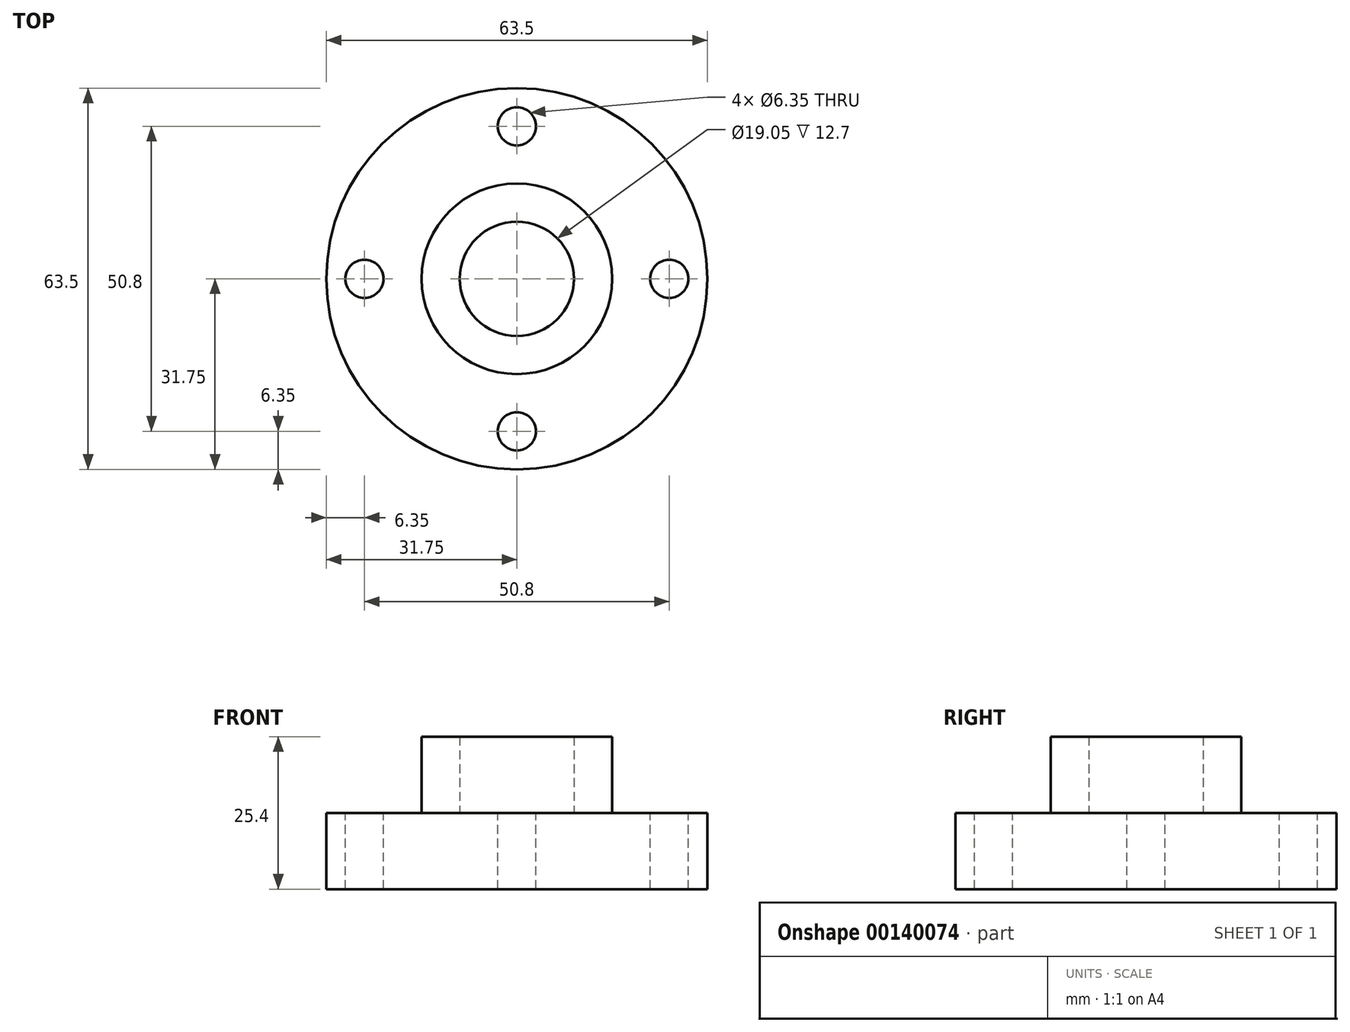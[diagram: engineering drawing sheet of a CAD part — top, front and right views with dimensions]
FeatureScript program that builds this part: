
annotation { "Feature Type Name" : "Feature", "Feature Type Description" : "" }
export const myFeature = defineFeature(function(context is Context, id is Id, definition is map)
    precondition{}
    {
        {
            var Q0;
            Q0=qCreatedBy(makeId("Top.planeOp"),FACE);
            var sketch = newSketch(context, id + "F0", { "sketchPlane" : qUnion([Q0])});
            skCircle(sketch, "E0", {"center": v(0, 0) * mm, "radius": 31.75 * mm});
            skSolve(sketch);
        }
        {
            var Q0;
            Q0 = qSketchRegion(id + "F0", true);
            extrude(context, id + "F1", {"entities" : qUnion([Q0]), "depth" : 12.7 * mm});
        }
        {
            var Q0;
            Q0=makeQuery(id+"F1.opExtrude","CAP_FACE",FACE,{"disambiguationData":[OSD([sQuery(id+"F0.wireOp",EDGE,"E0")])],"isStart":false});
            var sketch = newSketch(context, id + "F2", { "sketchPlane" : qUnion([Q0])});
            skCircle(sketch, "E1", {"center": v(0, 0) * mm, "radius": 15.88 * mm});
            skCircle(sketch, "E2", {"center": v(0, 0) * mm, "radius": 9.53 * mm});
            skCircle(sketch, "E3", {"center": v(-25.4, 0) * mm, "radius": 3.18 * mm});
            skCircle(sketch, "E4", {"center": v(0, 25.4) * mm, "radius": 3.18 * mm});
            skCircle(sketch, "E5", {"center": v(25.4, 0) * mm, "radius": 3.18 * mm});
            skCircle(sketch, "E6", {"center": v(0, -25.4) * mm, "radius": 3.18 * mm});
            skSolve(sketch);
        }
        {
            var Q0;
            Q0=makeQuery(id+"F2.imprint","IMPRINT",FACE,{"disambiguationData":[TD([[makeQuery(id+"F2.imprint","IMPRINT",EDGE,{"derivedFrom":sQuery(id+"F2.wireOp",EDGE,"E3")}),1.0]])]});
            var Q1;
            Q1=makeQuery(id+"F2.imprint","IMPRINT",FACE,{"disambiguationData":[TD([[makeQuery(id+"F2.imprint","IMPRINT",EDGE,{"derivedFrom":sQuery(id+"F2.wireOp",EDGE,"E6")}),1.0]])]});
            var Q2;
            Q2=makeQuery(id+"F2.imprint","IMPRINT",FACE,{"disambiguationData":[TD([[makeQuery(id+"F2.imprint","IMPRINT",EDGE,{"derivedFrom":sQuery(id+"F2.wireOp",EDGE,"E5")}),1.0]])]});
            var Q3;
            Q3=makeQuery(id+"F2.imprint","IMPRINT",FACE,{"disambiguationData":[TD([[makeQuery(id+"F2.imprint","IMPRINT",EDGE,{"derivedFrom":sQuery(id+"F2.wireOp",EDGE,"E4")}),1.0]])]});
            extrude(context, id + "F3", {"entities" : qUnion([Q0, Q1, Q2, Q3]), "operationType" : NewBodyOperationType.REMOVE, "endBound" : BoundingType.THROUGH_ALL, "oppositeDirection" : true, "depth" : 25.4 * mm});
        }
        {
            var Q0;
            Q0=makeQuery(id+"F2.imprint","IMPRINT",FACE,{"disambiguationData":[TD([[makeQuery(id+"F2.imprint","IMPRINT",EDGE,{"derivedFrom":sQuery(id+"F2.wireOp",EDGE,"E1")}),1.0]])]});
            extrude(context, id + "F4", {"entities" : qUnion([Q0]), "operationType" : NewBodyOperationType.ADD, "depth" : 12.7 * mm});
        }
    });
